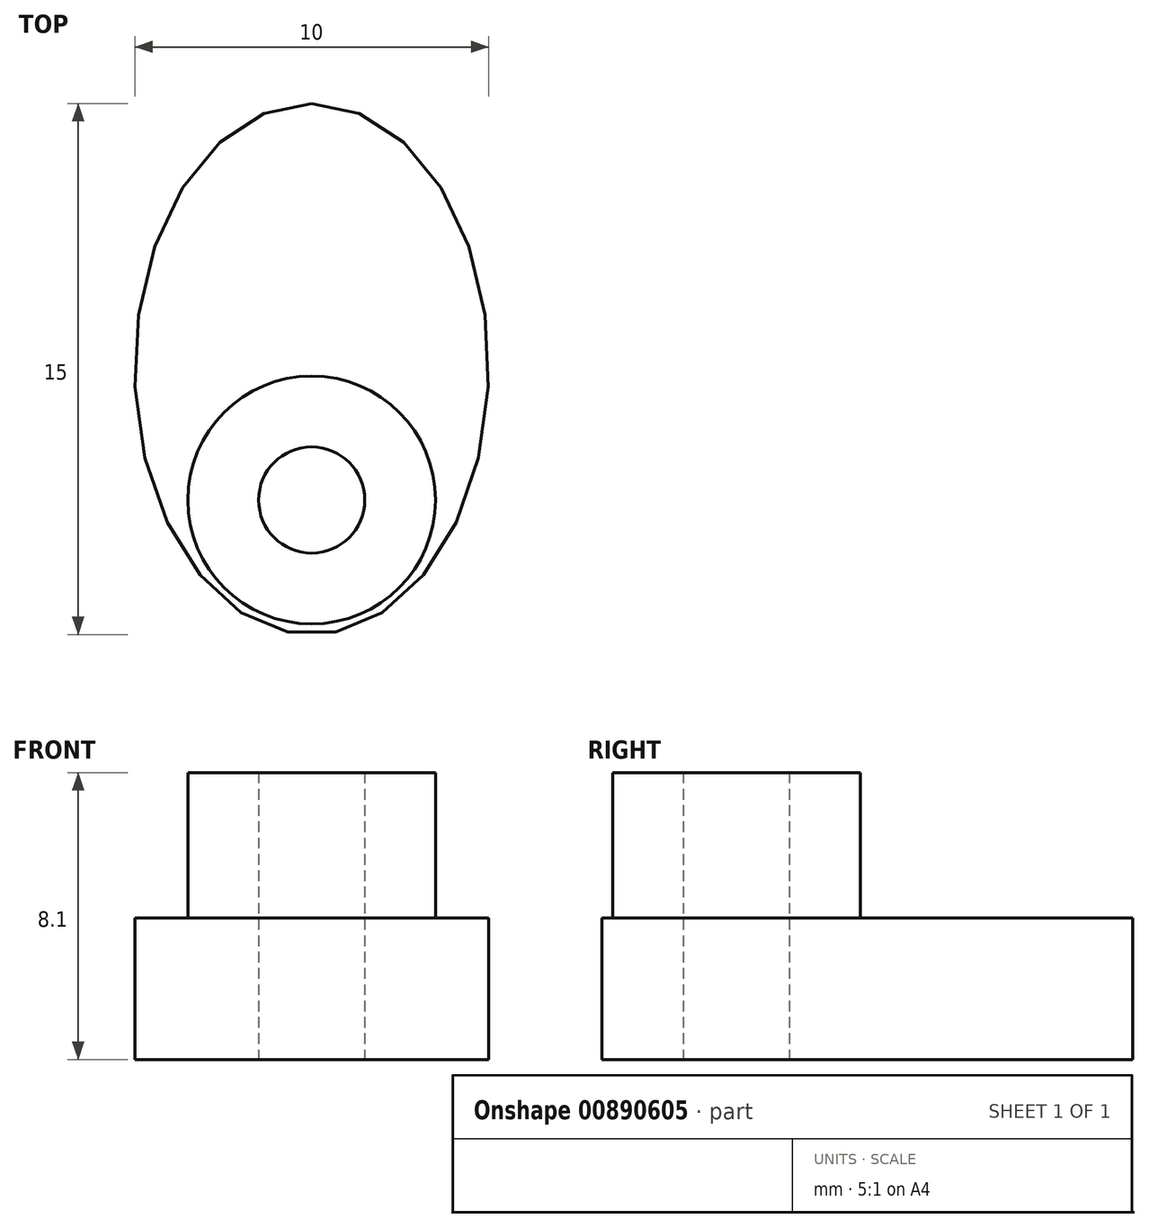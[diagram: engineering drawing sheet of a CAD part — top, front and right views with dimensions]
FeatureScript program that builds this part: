
annotation { "Feature Type Name" : "Feature", "Feature Type Description" : "" }
export const myFeature = defineFeature(function(context is Context, id is Id, definition is map)
    precondition{}
    {
        {
            var Q0;
            Q0=qCreatedBy(makeId("Top.planeOp"),FACE);
            var sketch = newSketch(context, id + "F0", { "sketchPlane" : qUnion([Q0])});
            skEllipse(sketch, "E0", {"center": v(0, 0) * mm, "majorRadius": 7.5 * mm, "minorRadius": 5 * mm, "majorAxis": v(0, 1)});
            skCircle(sketch, "E1", {"center": v(0, -3.7) * mm, "radius": 3.5 * mm});
            skCircle(sketch, "E2", {"center": v(0, -3.7) * mm, "radius": 1.5 * mm});
            skSolve(sketch);
        }
        {
            var Q0;
            Q0=makeQuery(id+"F0.imprint","IMPRINT",FACE,{"disambiguationData":[TD([[makeQuery(id+"F0.imprint","IMPRINT",EDGE,{"derivedFrom":sQuery(id+"F0.wireOp",EDGE,"E0")}),1.0]])]});
            extrude(context, id + "F1", {"entities" : qUnion([Q0]), "depth" : 4 * mm, "offsetDistance" : 25 * mm});
        }
        {
            var Q0;
            Q0=makeQuery(id+"F0.imprint","IMPRINT",FACE,{"disambiguationData":[TD([[makeQuery(id+"F0.imprint","IMPRINT",EDGE,{"derivedFrom":sQuery(id+"F0.wireOp",EDGE,"E1")}),1.0]])]});
            extrude(context, id + "F2", {"entities" : qUnion([Q0]), "operationType" : NewBodyOperationType.ADD, "depth" : 8.1 * mm, "offsetDistance" : 25 * mm});
        }
    });
